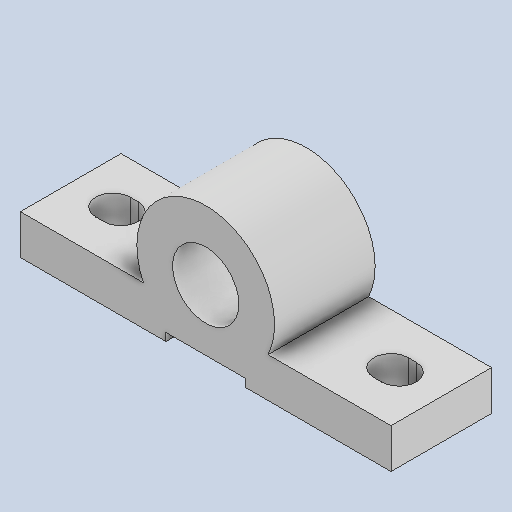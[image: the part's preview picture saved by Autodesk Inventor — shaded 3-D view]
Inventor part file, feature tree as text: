
AUTODESK INVENTOR PART (.ipt)
format: ipt  version: 2023 (Build 270158000, 158)  size: 269,312 bytes
history: native  units: mm
features: extrude x2, sketch x2, other x1
ambient origin geometry x8: Origin, YZ Plane, XZ Plane, XY Plane, X Axis, Y Axis, Z Axis, Center Point
bodies: Body1 (feature_tree)
feature tree (5):
  other  "Твердое тело1"
  extrude  "Выдавливание1"  Depth=25.0mm
  extrude  "Выдавливание2"  Depth=52.0mm
  sketch  "Эскиз1"
  sketch  "Эскиз2"
